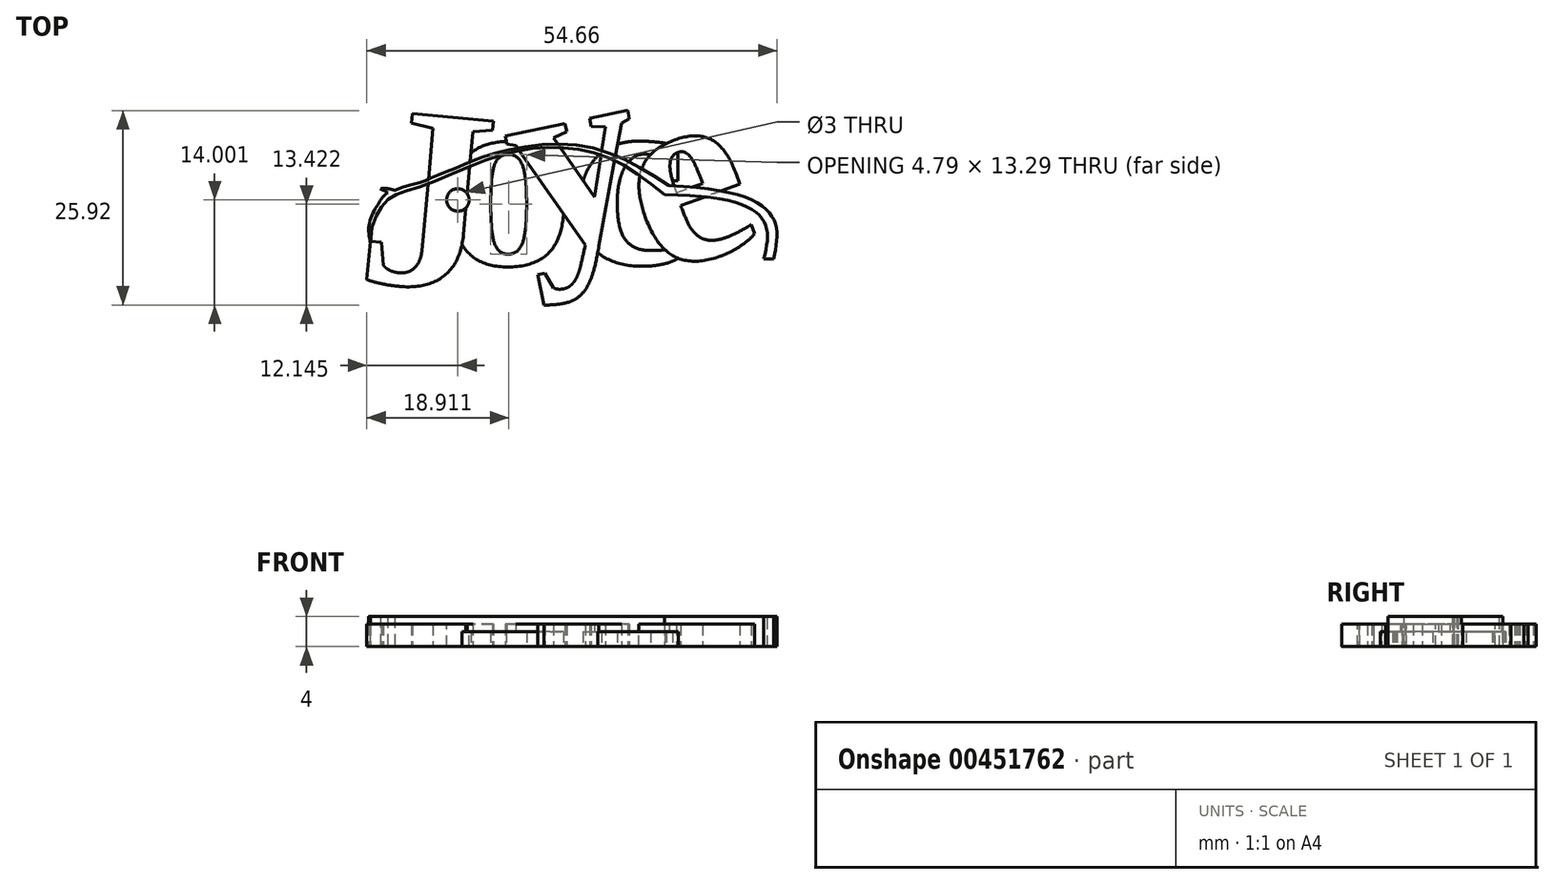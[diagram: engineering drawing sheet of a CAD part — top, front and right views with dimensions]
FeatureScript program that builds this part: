
annotation { "Feature Type Name" : "Feature", "Feature Type Description" : "" }
export const myFeature = defineFeature(function(context is Context, id is Id, definition is map)
    precondition{}
    {
        {
            var Q0;
            Q0=qCreatedBy(makeId("Top.planeOp"),FACE);
            var sketch = newSketch(context, id + "F0", { "sketchPlane" : qUnion([Q0])});
            skText(sketch, "E0", { "text": "J", "fontName": "Tinos-Bold.ttf"});
            skLineSegment(sketch, "E1", {"start": v(-63.23, 12.37) * mm, "end": v(-34.22, 41.11) * mm, "construction": true});
            const initialGuessF0  = {"E0": [-0.03697, -0.0089, 0.99578, -0.09177, 0.025]};
            skSetInitialGuess(sketch, initialGuessF0);
            skSolve(sketch);
        }
        {
            var Q0;
            Q0=qCreatedBy(makeId("Top.planeOp"),FACE);
            var sketch = newSketch(context, id + "F1", { "sketchPlane" : qUnion([Q0])});
            skText(sketch, "E2", { "text": "o", "fontName": "Tinos-Bold.ttf"});
            const initialGuessF1  = {"E2": [-0.02519, -0.00685, 1, 0, 0.025]};
            skSetInitialGuess(sketch, initialGuessF1);
            skSolve(sketch);
        }
        {
            var Q0;
            Q0=qCreatedBy(makeId("Top.planeOp"),FACE);
            var sketch = newSketch(context, id + "F2", { "sketchPlane" : qUnion([Q0])});
            skText(sketch, "E3", { "text": "y", "fontName": "Tinos-Bold.ttf"});
            skLineSegment(sketch, "E4", {"start": v(-5.12, -17.1) * mm, "end": v(19.2, 8.73) * mm, "construction": true});
            const initialGuessF2  = {"E3": [-0.01407, -0.00541, 0.97916, 0.20307, 0.025]};
            skSetInitialGuess(sketch, initialGuessF2);
            skSolve(sketch);
        }
        {
            var Q0;
            Q0=qCreatedBy(makeId("Top.planeOp"),FACE);
            var sketch = newSketch(context, id + "F3", { "sketchPlane" : qUnion([Q0])});
            skText(sketch, "E5", { "text": "c", "fontName": "Tinos-Bold.ttf"});
            const initialGuessF3  = {"E5": [-0.00816, -0.00679, 1, 0, 0.025]};
            skSetInitialGuess(sketch, initialGuessF3);
            skSolve(sketch);
        }
        {
            var Q0;
            Q0=qCreatedBy(makeId("Top.planeOp"),FACE);
            var sketch = newSketch(context, id + "F4", { "sketchPlane" : qUnion([Q0])});
            skText(sketch, "E6", { "text": "e", "fontName": "Tinos-Bold.ttf"});
            skLineSegment(sketch, "E7", {"start": v(6.56, -21.2) * mm, "end": v(25.28, 5.32) * mm, "construction": true});
            const initialGuessF4  = {"E6": [0.00328, -0.00846, 0.94105, 0.33826, 0.025]};
            skSetInitialGuess(sketch, initialGuessF4);
            skSolve(sketch);
        }
        {
            var Q0;
            Q0 = qSketchRegion(id + "F0", true);
            extrude(context, id + "F5", {"entities" : qUnion([Q0]), "depth" : 3 * mm});
        }
        {
            var Q0;
            Q0 = qSketchRegion(id + "F1", true);
            extrude(context, id + "F6", {"entities" : qUnion([Q0]), "operationType" : NewBodyOperationType.ADD, "depth" : 2 * mm});
        }
        {
            var Q0;
            Q0 = qSketchRegion(id + "F2", true);
            extrude(context, id + "F7", {"entities" : qUnion([Q0]), "operationType" : NewBodyOperationType.ADD, "depth" : 3 * mm});
        }
        {
            var Q0;
            Q0 = qSketchRegion(id + "F3", true);
            extrude(context, id + "F8", {"entities" : qUnion([Q0]), "operationType" : NewBodyOperationType.ADD, "depth" : 2 * mm});
        }
        {
            var Q0;
            Q0 = qSketchRegion(id + "F4", true);
            extrude(context, id + "F9", {"entities" : qUnion([Q0]), "operationType" : NewBodyOperationType.ADD, "depth" : 3 * mm});
        }
        {
            var Q0;
            Q0=makeQuery(id+"F5.opExtrude","CAP_FACE",FACE,{"disambiguationData":[OSD([sQuery(id+"F0.wireOp",EDGE,"E0.sketch_text.stroke-0"),sQuery(id+"F0.wireOp",EDGE,"E0.sketch_text.stroke-1"),sQuery(id+"F0.wireOp",EDGE,"E0.sketch_text.stroke-2"),sQuery(id+"F0.wireOp",EDGE,"E0.sketch_text.stroke-3"),sQuery(id+"F0.wireOp",EDGE,"E0.sketch_text.stroke-4"),sQuery(id+"F0.wireOp",EDGE,"E0.sketch_text.stroke-5"),sQuery(id+"F0.wireOp",EDGE,"E0.sketch_text.stroke-6"),sQuery(id+"F0.wireOp",EDGE,"E0.sketch_text.stroke-7"),sQuery(id+"F0.wireOp",EDGE,"E0.sketch_text.stroke-8"),sQuery(id+"F0.wireOp",EDGE,"E0.sketch_text.stroke-9"),sQuery(id+"F0.wireOp",EDGE,"E0.sketch_text.stroke-10"),sQuery(id+"F0.wireOp",EDGE,"E0.sketch_text.stroke-11"),sQuery(id+"F0.wireOp",EDGE,"E0.sketch_text.stroke-12"),sQuery(id+"F0.wireOp",EDGE,"E0.sketch_text.stroke-13"),sQuery(id+"F0.wireOp",EDGE,"E0.sketch_text.stroke-14"),sQuery(id+"F0.wireOp",EDGE,"E0.sketch_text.stroke-15"),sQuery(id+"F0.wireOp",EDGE,"E0.sketch_text.stroke-16"),sQuery(id+"F0.wireOp",EDGE,"E0.sketch_text.stroke-17")])],"isStart":false});
            var sketch = newSketch(context, id + "F10", { "sketchPlane" : qUnion([Q0])});
            skCircle(sketch, "E8", {"center": v(-23.27, 1.73) * mm, "radius": 1.5 * mm});
            skSolve(sketch);
        }
        {
            var Q0;
            Q0 = qSketchRegion(id + "F10", true);
            extrude(context, id + "F11", {"entities" : qUnion([Q0]), "operationType" : NewBodyOperationType.REMOVE, "endBound" : BoundingType.THROUGH_ALL, "oppositeDirection" : true, "depth" : 25 * mm});
        }
        {
            var Q0;
            Q0=qCreatedBy(makeId("Top.planeOp"),FACE);
            var sketch = newSketch(context, id + "F12", { "sketchPlane" : qUnion([Q0])});
            skLineSegment(sketch, "E9", {"start": v(17.46, -6.12) * mm, "end": v(18.8, -6.12) * mm});
            skFitSpline(sketch, "E10", {"points": [v(-33.57, 3.21) * mm, v(-32.64, 2.7) * mm], "startDerivative": vector(0, -0.31) * mm, "endDerivative": vector(1.68, -1.27) * mm});
            skFitSpline(sketch, "E11", {"points": [v(-33.57, 3.21) * mm, v(-31.68, 3.02) * mm], "startDerivative": vector(1.85, 0.55) * mm, "endDerivative": vector(1.27, -0.3) * mm});
            skFitSpline(sketch, "E12", {"points": [v(-32.64, 2.7) * mm, v(-33.92, 1.18) * mm, v(-35.08, -1.36) * mm, v(-34.9, -4.01) * mm], "startDerivative": vector(-6.8, -4.66) * mm, "endDerivative": vector(1.66, -7.4) * mm});
            skFitSpline(sketch, "E13", {"points": [v(17.46, -6.12) * mm, v(4.25, 2.44) * mm], "startDerivative": vector(4.1, 14.54) * mm, "endDerivative": vector(-42.36, 0.45) * mm});
            skFitSpline(sketch, "E14", {"points": [v(18.8, -6.12) * mm, v(4.84, 3.65) * mm], "startDerivative": vector(3.14, 14.07) * mm, "endDerivative": vector(-46.47, 2.02) * mm});
            skFitSpline(sketch, "E15", {"points": [v(4.84, 3.65) * mm, v(-6.92, 8.97) * mm, v(-18.8, 7.81) * mm, v(-23.5, 6.02) * mm, v(-26.72, 4.71) * mm, v(-28.45, 4) * mm, v(-31.68, 3.02) * mm], "startDerivative": vector(-45.36, 29.8) * mm, "endDerivative": vector(-26.51, -11.83) * mm});
            skFitSpline(sketch, "E16", {"points": [v(4.25, 2.44) * mm, v(-1.88, 6.76) * mm, v(-8.1, 8.58) * mm, v(-14.33, 8.44) * mm, v(-21.24, 6.38) * mm, v(-28.78, 3.32) * mm, v(-32.05, 2.2) * mm, v(-33.77, 0.32) * mm, v(-34.9, -4.01) * mm], "startDerivative": vector(-39.42, 31.72) * mm, "endDerivative": vector(2.59, -54.22) * mm});
            skSolve(sketch);
        }
        {
            var Q0;
            Q0 = qSketchRegion(id + "F12", true);
            extrude(context, id + "F13", {"entities" : qUnion([Q0]), "depth" : 4 * mm, "offsetDistance" : 25 * mm});
        }
    });
